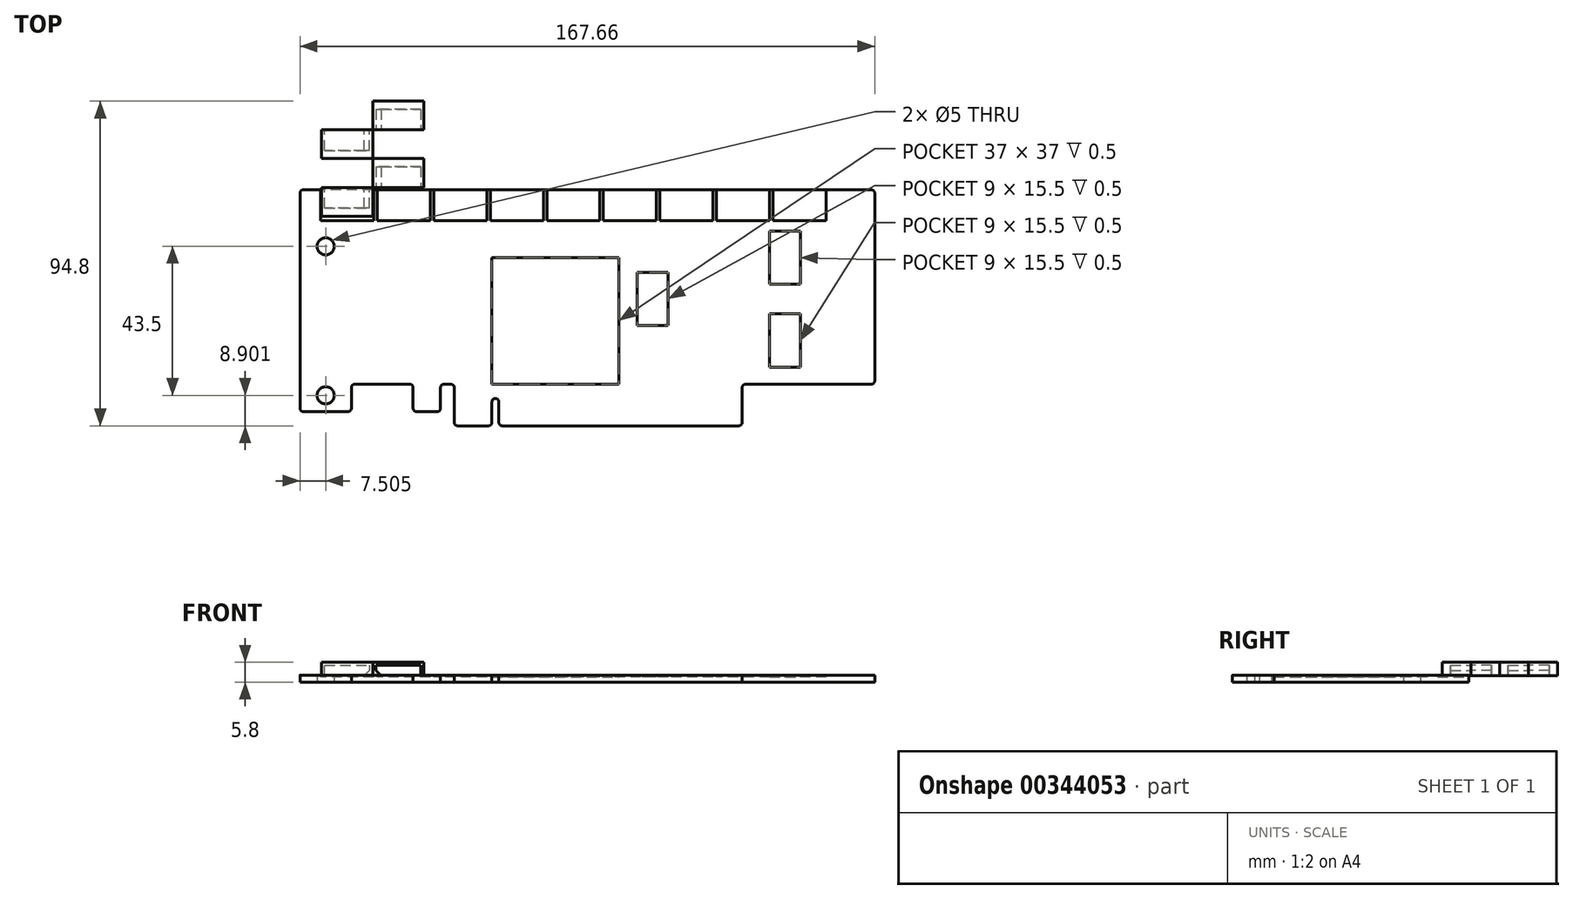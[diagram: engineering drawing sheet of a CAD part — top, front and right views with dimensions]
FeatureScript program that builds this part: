
annotation { "Feature Type Name" : "Feature", "Feature Type Description" : "" }
export const myFeature = defineFeature(function(context is Context, id is Id, definition is map)
    precondition{}
    {
        {
            var Q0;
            Q0=qCreatedBy(makeId("Top.planeOp"),FACE);
            var sketch = newSketch(context, id + "F0", { "sketchPlane" : qUnion([Q0])});
            skLineSegment(sketch, "E0.top", {"start": v(83.83, 32.37) * mm, "end": v(-83.83, 32.37) * mm});
            skLineSegment(sketch, "E0.right", {"start": v(-83.83, -32.37) * mm, "end": v(-83.83, 32.37) * mm});
            skPoint(sketch, "E0.middle", {"position": v(0, 0) * mm});
            skLineSegment(sketch, "E1", {"start": v(-83.83, -32.37) * mm, "end": v(-68.83, -32.37) * mm});
            skLineSegment(sketch, "E2", {"start": v(-68.83, -32.37) * mm, "end": v(-68.83, -24.37) * mm});
            skLineSegment(sketch, "E3", {"start": v(-68.83, -24.37) * mm, "end": v(-50.82, -24.37) * mm});
            skLineSegment(sketch, "E4", {"start": v(-50.82, -24.37) * mm, "end": v(-50.82, -32.37) * mm});
            skLineSegment(sketch, "E5", {"start": v(-50.82, -32.37) * mm, "end": v(-42.83, -32.37) * mm});
            skLineSegment(sketch, "E6", {"start": v(-42.83, -32.37) * mm, "end": v(-42.82, -24.37) * mm});
            skLineSegment(sketch, "E7", {"start": v(-42.82, -24.37) * mm, "end": v(-38.82, -24.37) * mm});
            skLineSegment(sketch, "E8", {"start": v(-38.82, -24.37) * mm, "end": v(-38.82, -36.53) * mm});
            skLineSegment(sketch, "E9", {"start": v(-38.82, -36.53) * mm, "end": v(-27.82, -36.53) * mm});
            skLineSegment(sketch, "E10", {"start": v(-27.82, -36.53) * mm, "end": v(-27.82, -28.53) * mm});
            skLineSegment(sketch, "E11", {"start": v(-27.82, -28.53) * mm, "end": v(-25.82, -28.53) * mm});
            skLineSegment(sketch, "E12", {"start": v(-25.82, -28.53) * mm, "end": v(-25.82, -36.53) * mm});
            skLineSegment(sketch, "E13", {"start": v(-25.82, -36.53) * mm, "end": v(45.18, -36.53) * mm});
            skLineSegment(sketch, "E14", {"start": v(45.18, -36.53) * mm, "end": v(45.18, -24.37) * mm});
            skLineSegment(sketch, "E15", {"start": v(83.83, 32.37) * mm, "end": v(83.83, -24.37) * mm});
            skCircle(sketch, "E16", {"center": v(-76.33, -27.63) * mm, "radius": 2.5 * mm});
            skCircle(sketch, "E17.MirrorC", {"center": v(-76.33, 15.87) * mm, "radius": 2.5 * mm});
            skLineSegment(sketch, "E18", {"start": v(45.18, -24.37) * mm, "end": v(83.82, -24.37) * mm});
            skLineSegment(sketch, "E19", {"start": v(-76.33, 15.87) * mm, "end": v(-76.33, -27.63) * mm, "construction": true});
            skLineSegment(sketch, "E20", {"start": v(-76.33, 15.87) * mm, "end": v(-76.33, 32.37) * mm, "construction": true});
            skLineSegment(sketch, "E21", {"start": v(-83.83, 0) * mm, "end": v(-76.33, 0) * mm, "construction": true});
            skSolve(sketch);
        }
        {
            var Q0;
            Q0=qSketchRegion(id+"F0",true);
            extrude(context, id + "F1", {"entities" : qUnion([Q0]), "depth" : 2 * mm});
        }
        {
            var Q0;
            Q0=makeQuery(id+"F1.opExtrude","CAP_FACE",FACE,{"disambiguationData":[OSD([sQuery(id+"F0.wireOp",EDGE,"E0.top"),sQuery(id+"F0.wireOp",EDGE,"E0.right"),sQuery(id+"F0.wireOp",EDGE,"E1"),sQuery(id+"F0.wireOp",EDGE,"E2"),sQuery(id+"F0.wireOp",EDGE,"E3"),sQuery(id+"F0.wireOp",EDGE,"E4"),sQuery(id+"F0.wireOp",EDGE,"E5"),sQuery(id+"F0.wireOp",EDGE,"E6"),sQuery(id+"F0.wireOp",EDGE,"E7"),sQuery(id+"F0.wireOp",EDGE,"E8"),sQuery(id+"F0.wireOp",EDGE,"E9"),sQuery(id+"F0.wireOp",EDGE,"E10"),sQuery(id+"F0.wireOp",EDGE,"E11"),sQuery(id+"F0.wireOp",EDGE,"E12"),sQuery(id+"F0.wireOp",EDGE,"E13"),sQuery(id+"F0.wireOp",EDGE,"E14"),sQuery(id+"F0.wireOp",EDGE,"E15"),sQuery(id+"F0.wireOp",EDGE,"E16"),sQuery(id+"F0.wireOp",EDGE,"E17.MirrorC"),sQuery(id+"F0.wireOp",EDGE,"E18")])],"isStart":false});
            var sketch = newSketch(context, id + "F2", { "sketchPlane" : qUnion([Q0])});
            skLineSegment(sketch, "E22.bottom", {"start": v(-77.83, 23.37) * mm, "end": v(-62.33, 23.37) * mm});
            skLineSegment(sketch, "E22.top", {"start": v(-77.83, 32.37) * mm, "end": v(-62.33, 32.37) * mm});
            skLineSegment(sketch, "E22.left", {"start": v(-77.83, 23.37) * mm, "end": v(-77.83, 32.37) * mm});
            skLineSegment(sketch, "E22.right", {"start": v(-62.33, 23.37) * mm, "end": v(-62.33, 32.37) * mm});
            skLineSegment(sketch, "E23", {"start": v(-77.83, 32.37) * mm, "end": v(-83.83, 32.37) * mm, "construction": true});
            skLineSegment(sketch, "E24.1.0.0", {"start": v(-61.33, 32.37) * mm, "end": v(-45.83, 32.37) * mm});
            skLineSegment(sketch, "E24.1.0.1", {"start": v(-61.33, 23.37) * mm, "end": v(-61.33, 32.37) * mm});
            skLineSegment(sketch, "E24.1.0.2", {"start": v(-61.33, 23.37) * mm, "end": v(-45.83, 23.37) * mm});
            skLineSegment(sketch, "E24.1.0.3", {"start": v(-45.83, 23.37) * mm, "end": v(-45.83, 32.37) * mm});
            skLineSegment(sketch, "E24.2.0.0", {"start": v(-44.83, 32.37) * mm, "end": v(-29.33, 32.37) * mm});
            skLineSegment(sketch, "E24.2.0.1", {"start": v(-44.83, 23.37) * mm, "end": v(-44.83, 32.37) * mm});
            skLineSegment(sketch, "E24.2.0.2", {"start": v(-44.83, 23.37) * mm, "end": v(-29.33, 23.37) * mm});
            skLineSegment(sketch, "E24.2.0.3", {"start": v(-29.33, 23.37) * mm, "end": v(-29.33, 32.37) * mm});
            skLineSegment(sketch, "E24.direction1", {"start": v(-77.83, 32.37) * mm, "end": v(-61.33, 32.37) * mm, "construction": true});
            skLineSegment(sketch, "E25.0.3.0", {"start": v(-28.33, 32.37) * mm, "end": v(-12.83, 32.37) * mm});
            skLineSegment(sketch, "E25.3.3.0", {"start": v(-28.33, 23.37) * mm, "end": v(-28.33, 32.37) * mm});
            skLineSegment(sketch, "E25.6.3.0", {"start": v(-28.33, 23.37) * mm, "end": v(-12.83, 23.37) * mm});
            skLineSegment(sketch, "E25.9.3.0", {"start": v(-12.83, 23.37) * mm, "end": v(-12.83, 32.37) * mm});
            skLineSegment(sketch, "E25.0.4.0", {"start": v(-11.83, 32.37) * mm, "end": v(3.67, 32.37) * mm});
            skLineSegment(sketch, "E25.3.4.0", {"start": v(-11.83, 23.37) * mm, "end": v(-11.83, 32.37) * mm});
            skLineSegment(sketch, "E25.6.4.0", {"start": v(-11.83, 23.37) * mm, "end": v(3.67, 23.37) * mm});
            skLineSegment(sketch, "E25.9.4.0", {"start": v(3.67, 23.37) * mm, "end": v(3.67, 32.37) * mm});
            skLineSegment(sketch, "E25.0.5.0", {"start": v(4.67, 32.37) * mm, "end": v(20.17, 32.37) * mm});
            skLineSegment(sketch, "E25.3.5.0", {"start": v(4.67, 23.37) * mm, "end": v(4.67, 32.37) * mm});
            skLineSegment(sketch, "E25.6.5.0", {"start": v(4.67, 23.37) * mm, "end": v(20.17, 23.37) * mm});
            skLineSegment(sketch, "E25.9.5.0", {"start": v(20.17, 23.37) * mm, "end": v(20.17, 32.37) * mm});
            skLineSegment(sketch, "E25.0.6.0", {"start": v(21.17, 32.37) * mm, "end": v(36.67, 32.37) * mm});
            skLineSegment(sketch, "E25.3.6.0", {"start": v(21.17, 23.37) * mm, "end": v(21.17, 32.37) * mm});
            skLineSegment(sketch, "E25.6.6.0", {"start": v(21.17, 23.37) * mm, "end": v(36.67, 23.37) * mm});
            skLineSegment(sketch, "E25.9.6.0", {"start": v(36.67, 23.37) * mm, "end": v(36.67, 32.37) * mm});
            skLineSegment(sketch, "E25.0.7.0", {"start": v(37.67, 32.37) * mm, "end": v(53.17, 32.37) * mm});
            skLineSegment(sketch, "E25.3.7.0", {"start": v(37.67, 23.37) * mm, "end": v(37.67, 32.37) * mm});
            skLineSegment(sketch, "E25.6.7.0", {"start": v(37.67, 23.37) * mm, "end": v(53.17, 23.37) * mm});
            skLineSegment(sketch, "E25.9.7.0", {"start": v(53.17, 23.37) * mm, "end": v(53.17, 32.37) * mm});
            skLineSegment(sketch, "E25.0.8.0", {"start": v(54.17, 32.37) * mm, "end": v(69.67, 32.37) * mm});
            skLineSegment(sketch, "E25.3.8.0", {"start": v(54.17, 23.37) * mm, "end": v(54.17, 32.37) * mm});
            skLineSegment(sketch, "E25.6.8.0", {"start": v(54.17, 23.37) * mm, "end": v(69.67, 23.37) * mm});
            skLineSegment(sketch, "E25.9.8.0", {"start": v(69.67, 23.37) * mm, "end": v(69.67, 32.37) * mm});
            skLineSegment(sketch, "E26", {"start": v(53.17, 23.37) * mm, "end": v(53.17, 20.37) * mm, "construction": true});
            skLineSegment(sketch, "E27.bottom", {"start": v(53.17, 20.37) * mm, "end": v(62.17, 20.37) * mm});
            skLineSegment(sketch, "E27.top", {"start": v(53.17, 4.87) * mm, "end": v(62.17, 4.87) * mm});
            skLineSegment(sketch, "E27.left", {"start": v(53.17, 20.37) * mm, "end": v(53.17, 4.87) * mm});
            skLineSegment(sketch, "E27.right", {"start": v(62.17, 20.37) * mm, "end": v(62.17, 4.87) * mm});
            skLineSegment(sketch, "E28.bottom", {"start": v(53.17, -19.37) * mm, "end": v(62.17, -19.37) * mm});
            skLineSegment(sketch, "E28.top", {"start": v(53.17, -3.87) * mm, "end": v(62.17, -3.87) * mm});
            skLineSegment(sketch, "E28.left", {"start": v(53.17, -19.37) * mm, "end": v(53.17, -3.87) * mm});
            skLineSegment(sketch, "E28.right", {"start": v(62.17, -19.37) * mm, "end": v(62.17, -3.87) * mm});
            skLineSegment(sketch, "E29", {"start": v(53.17, 4.87) * mm, "end": v(53.17, -3.87) * mm, "construction": true});
            skLineSegment(sketch, "E30", {"start": v(53.17, -19.37) * mm, "end": v(53.17, -24.37) * mm, "construction": true});
            skLineSegment(sketch, "E31", {"start": v(53.17, 0.5) * mm, "end": v(23.53, 0.5) * mm, "construction": true});
            skLineSegment(sketch, "E32.bottom", {"start": v(23.53, 8.25) * mm, "end": v(14.53, 8.25) * mm});
            skLineSegment(sketch, "E32.top", {"start": v(23.53, -7.25) * mm, "end": v(14.53, -7.25) * mm});
            skLineSegment(sketch, "E32.left", {"start": v(23.53, 8.25) * mm, "end": v(23.53, -7.25) * mm});
            skLineSegment(sketch, "E32.right", {"start": v(14.53, 8.25) * mm, "end": v(14.53, -7.25) * mm});
            skLineSegment(sketch, "E33.bottom", {"start": v(-27.82, -24.37) * mm, "end": v(9.18, -24.37) * mm});
            skLineSegment(sketch, "E33.top", {"start": v(-27.82, 12.63) * mm, "end": v(9.18, 12.63) * mm});
            skLineSegment(sketch, "E33.left", {"start": v(-27.82, -24.37) * mm, "end": v(-27.82, 12.63) * mm});
            skLineSegment(sketch, "E33.right", {"start": v(9.18, -24.37) * mm, "end": v(9.18, 12.63) * mm});
            skLineSegment(sketch, "E34", {"start": v(-38.82, -24.37) * mm, "end": v(-27.82, -24.37) * mm, "construction": true});
            skSolve(sketch);
        }
        {
            var Q0;
            Q0=makeQuery(id+"F1.opExtrude","SWEPT_EDGE",EDGE,{"disambiguationData":[OSD([sQuery(id+"F0.wireOp",EDGE,"E0.right"),sQuery(id+"F0.wireOp",EDGE,"E1")])]});
            var Q1;
            Q1=makeQuery(id+"F1.opExtrude","SWEPT_EDGE",EDGE,{"disambiguationData":[OSD([sQuery(id+"F0.wireOp",EDGE,"E1"),sQuery(id+"F0.wireOp",EDGE,"E2")])]});
            var Q2;
            Q2=makeQuery(id+"F1.opExtrude","SWEPT_EDGE",EDGE,{"disambiguationData":[OSD([sQuery(id+"F0.wireOp",EDGE,"E2"),sQuery(id+"F0.wireOp",EDGE,"E3")])]});
            var Q3;
            Q3=makeQuery(id+"F1.opExtrude","SWEPT_EDGE",EDGE,{"disambiguationData":[OSD([sQuery(id+"F0.wireOp",EDGE,"E4"),sQuery(id+"F0.wireOp",EDGE,"E5")])]});
            var Q4;
            Q4=makeQuery(id+"F1.opExtrude","SWEPT_EDGE",EDGE,{"disambiguationData":[OSD([sQuery(id+"F0.wireOp",EDGE,"E5"),sQuery(id+"F0.wireOp",EDGE,"E6")])]});
            var Q5;
            Q5=makeQuery(id+"F1.opExtrude","SWEPT_EDGE",EDGE,{"disambiguationData":[OSD([sQuery(id+"F0.wireOp",EDGE,"E6"),sQuery(id+"F0.wireOp",EDGE,"E7")])]});
            var Q6;
            Q6=makeQuery(id+"F1.opExtrude","SWEPT_EDGE",EDGE,{"disambiguationData":[OSD([sQuery(id+"F0.wireOp",EDGE,"E8"),sQuery(id+"F0.wireOp",EDGE,"E9")])]});
            var Q7;
            Q7=makeQuery(id+"F1.opExtrude","SWEPT_EDGE",EDGE,{"disambiguationData":[OSD([sQuery(id+"F0.wireOp",EDGE,"E9"),sQuery(id+"F0.wireOp",EDGE,"E10")])]});
            var Q8;
            Q8=makeQuery(id+"F1.opExtrude","SWEPT_EDGE",EDGE,{"disambiguationData":[OSD([sQuery(id+"F0.wireOp",EDGE,"E10"),sQuery(id+"F0.wireOp",EDGE,"E11")])]});
            var Q9;
            Q9=makeQuery(id+"F1.opExtrude","SWEPT_EDGE",EDGE,{"disambiguationData":[OSD([sQuery(id+"F0.wireOp",EDGE,"E12"),sQuery(id+"F0.wireOp",EDGE,"E13")])]});
            var Q10;
            Q10=makeQuery(id+"F1.opExtrude","SWEPT_EDGE",EDGE,{"disambiguationData":[OSD([sQuery(id+"F0.wireOp",EDGE,"E15"),sQuery(id+"F0.wireOp",EDGE,"E18")])]});
            var Q11;
            Q11=makeQuery(id+"F1.opExtrude","SWEPT_EDGE",EDGE,{"disambiguationData":[OSD([sQuery(id+"F0.wireOp",EDGE,"E14"),sQuery(id+"F0.wireOp",EDGE,"E18")])]});
            var Q12;
            Q12=makeQuery(id+"F1.opExtrude","SWEPT_EDGE",EDGE,{"disambiguationData":[OSD([sQuery(id+"F0.wireOp",EDGE,"E13"),sQuery(id+"F0.wireOp",EDGE,"E14")])]});
            var Q13;
            Q13=makeQuery(id+"F1.opExtrude","SWEPT_EDGE",EDGE,{"disambiguationData":[OSD([sQuery(id+"F0.wireOp",EDGE,"E0.top"),sQuery(id+"F0.wireOp",EDGE,"E15")])]});
            var Q14;
            Q14=makeQuery(id+"F1.opExtrude","SWEPT_EDGE",EDGE,{"disambiguationData":[OSD([sQuery(id+"F0.wireOp",EDGE,"E0.top"),sQuery(id+"F0.wireOp",EDGE,"E0.right")])]});
            var Q15;
            Q15=makeQuery(id+"F1.opExtrude","SWEPT_EDGE",EDGE,{"disambiguationData":[OSD([sQuery(id+"F0.wireOp",EDGE,"E3"),sQuery(id+"F0.wireOp",EDGE,"E4")])]});
            var Q16;
            Q16=makeQuery(id+"F1.opExtrude","SWEPT_EDGE",EDGE,{"disambiguationData":[OSD([sQuery(id+"F0.wireOp",EDGE,"E7"),sQuery(id+"F0.wireOp",EDGE,"E8")])]});
            var Q17;
            Q17=makeQuery(id+"F1.opExtrude","SWEPT_EDGE",EDGE,{"disambiguationData":[OSD([sQuery(id+"F0.wireOp",EDGE,"E11"),sQuery(id+"F0.wireOp",EDGE,"E12")])]});
            fillet(context, id + "F3", {"entities" : qUnion([Q0, Q1, Q2, Q3, Q4, Q5, Q6, Q7, Q8, Q9, Q10, Q11, Q12, Q13, Q14, Q15, Q16, Q17]), "radius" : 1 * mm, "tangentPropagation" : true, "allowEdgeOverflow" : false});
        }
        {
            var Q0;
            Q0 = qSketchRegion(id + "F2", true);
            extrude(context, id + "F4", {"entities" : qUnion([Q0]), "operationType" : NewBodyOperationType.REMOVE, "oppositeDirection" : true, "depth" : .5 * mm});
        }
        {
            var Q0;
            Q0=makeQuery(id+"F4.boolean.opBoolean","COPY",FACE,{"derivedFrom":makeQuery(id+"F4.opExtrude","CAP_FACE",FACE,{"disambiguationData":[OSD([sQuery(id+"F2.wireOp",EDGE,"E22.bottom"),sQuery(id+"F2.wireOp",EDGE,"E22.top"),sQuery(id+"F2.wireOp",EDGE,"E22.left"),sQuery(id+"F2.wireOp",EDGE,"E22.right")])],"isStart":false})});
            cPlane(context, id + "F5", {"entities" : qUnion([Q0]), "cplaneType" : CPlaneType.OFFSET, "offset" : .3 * mm, "width" : 150 * mm, "height" : 150 * mm});
        }
        {
            var Q0;
            Q0=qCreatedBy(id+"F5.planeOp",FACE);
            var sketch = newSketch(context, id + "F6", { "sketchPlane" : qUnion([Q0])});
            skLineSegment(sketch, "E35.0", {"start": v(-77.83, 23.37) * mm, "end": v(-77.83, 32.37) * mm, "construction": true});
            skLineSegment(sketch, "E36.0", {"start": v(-77.83, 23.37) * mm, "end": v(-62.33, 23.37) * mm, "construction": true});
            skLineSegment(sketch, "E37.0", {"start": v(-62.33, 23.37) * mm, "end": v(-62.33, 32.37) * mm, "construction": true});
            skLineSegment(sketch, "E38.0", {"start": v(-62.33, 32.37) * mm, "end": v(-77.83, 32.37) * mm, "construction": true});
            skLineSegment(sketch, "E39.0", {"start": v(-62.63, 32.07) * mm, "end": v(-77.53, 32.07) * mm});
            skLineSegment(sketch, "E39.1", {"start": v(-62.63, 23.67) * mm, "end": v(-62.63, 32.07) * mm});
            skLineSegment(sketch, "E39.2", {"start": v(-77.53, 23.67) * mm, "end": v(-62.63, 23.67) * mm});
            skLineSegment(sketch, "E39.3", {"start": v(-77.53, 23.67) * mm, "end": v(-77.53, 32.07) * mm});
            skSolve(sketch);
        }
        {
            var Q0;
            Q0 = qSketchRegion(id + "F6", true);
            extrude(context, id + "F7", {"entities" : qUnion([Q0]), "depth" : 4 * mm});
        }
        {
            var Q0;
            Q0=makeQuery(id+"F7.opExtrude","SWEPT_FACE",FACE,{"disambiguationData":[OSD([sQuery(id+"F6.wireOp",EDGE,"E39.0")])]});
            var sketch = newSketch(context, id + "F8", { "sketchPlane" : qUnion([Q0])});
            skLineSegment(sketch, "E40", {"start": v(76.63, 1.8) * mm, "end": v(76.63, 4.9) * mm});
            skLineSegment(sketch, "E41", {"start": v(76.63, 4.9) * mm, "end": v(63.53, 4.9) * mm});
            skLineSegment(sketch, "E42", {"start": v(63.53, 4.9) * mm, "end": v(63.53, 3.4) * mm});
            skLineSegment(sketch, "E43", {"start": v(63.53, 3.4) * mm, "end": v(65.13, 1.8) * mm});
            skLineSegment(sketch, "E44", {"start": v(65.13, 1.8) * mm, "end": v(76.63, 1.8) * mm});
            skLineSegment(sketch, "E45", {"start": v(70.08, 5.8) * mm, "end": v(70.08, 4.9) * mm, "construction": true});
            skSolve(sketch);
        }
        {
            var Q0;
            Q0 = qSketchRegion(id + "F8", true);
            extrude(context, id + "F9", {"entities" : qUnion([Q0]), "operationType" : NewBodyOperationType.REMOVE, "oppositeDirection" : true, "depth" : 6 * mm});
        }
        {
            var Q0;
            Q0=makeQuery(id+"F7.opExtrude","SWEPT_BODY",BODY,{"disambiguationData":[OSD([sQuery(id+"F6.wireOp",EDGE,"E39.0"),sQuery(id+"F6.wireOp",EDGE,"E39.1"),sQuery(id+"F6.wireOp",EDGE,"E39.2"),sQuery(id+"F6.wireOp",EDGE,"E39.3")])]});
            transform(context, id + "F10", {"entities" : qUnion([Q0]), "transformType" : TransformType.TRANSLATION_3D, "dx" : 0 * mm, "dy" : 1 * mm, "dz" : 0 * mm, "makeCopy" : false});
        }
        {
            var Q0;
            Q0=makeQuery(id+"F7.opExtrude","SWEPT_BODY",BODY,{"disambiguationData":[OSD([sQuery(id+"F6.wireOp",EDGE,"E39.0"),sQuery(id+"F6.wireOp",EDGE,"E39.1"),sQuery(id+"F6.wireOp",EDGE,"E39.2"),sQuery(id+"F6.wireOp",EDGE,"E39.3")])]});
            var Q1;
            Q1=makeQuery(id+"F7.opExtrude","SWEPT_EDGE",EDGE,{"disambiguationData":[OSD([sQuery(id+"F6.wireOp",EDGE,"E39.0"),sQuery(id+"F6.wireOp",EDGE,"E39.1")])]});
            transform(context, id + "F11", {"entities" : qUnion([Q0]), "transformType" : TransformType.ROTATION, "transformAxis" : qUnion([Q1]), "angle" : 180 * degree, "makeCopy" : true});
        }
        {
            var Q0;
            Q0=makeQuery(id+"F11.opPattern","COPY",BODY,{"derivedFrom":makeQuery(id+"F7.opExtrude","SWEPT_BODY",BODY,{"disambiguationData":[OSD([sQuery(id+"F6.wireOp",EDGE,"E39.0"),sQuery(id+"F6.wireOp",EDGE,"E39.1"),sQuery(id+"F6.wireOp",EDGE,"E39.2"),sQuery(id+"F6.wireOp",EDGE,"E39.3")])]}),"instanceName":"1"});
            var Q1;
            Q1=makeQuery(id+"F11.opPattern","COPY",EDGE,{"derivedFrom":makeQuery(id+"F7.opExtrude","SWEPT_EDGE",EDGE,{"disambiguationData":[OSD([sQuery(id+"F6.wireOp",EDGE,"E39.1"),sQuery(id+"F6.wireOp",EDGE,"E39.2")])]}),"instanceName":"1"});
            transform(context, id + "F12", {"entities" : qUnion([Q0]), "transformType" : TransformType.ROTATION, "transformAxis" : qUnion([Q1]), "angle" : 180 * degree, "makeCopy" : true});
        }
        {
            var Q0;
            Q0=makeQuery(id+"F12.opPattern","COPY",BODY,{"derivedFrom":makeQuery(id+"F11.opPattern","COPY",BODY,{"derivedFrom":makeQuery(id+"F7.opExtrude","SWEPT_BODY",BODY,{"disambiguationData":[OSD([sQuery(id+"F6.wireOp",EDGE,"E39.0"),sQuery(id+"F6.wireOp",EDGE,"E39.1"),sQuery(id+"F6.wireOp",EDGE,"E39.2"),sQuery(id+"F6.wireOp",EDGE,"E39.3")])]}),"instanceName":"1"}),"instanceName":"1"});
            var Q1;
            Q1=makeQuery(id+"F12.opPattern","COPY",EDGE,{"derivedFrom":makeQuery(id+"F11.opPattern","COPY",EDGE,{"derivedFrom":makeQuery(id+"F7.opExtrude","SWEPT_EDGE",EDGE,{"disambiguationData":[OSD([sQuery(id+"F6.wireOp",EDGE,"E39.0"),sQuery(id+"F6.wireOp",EDGE,"E39.1")])]}),"instanceName":"1"}),"instanceName":"1"});
            transform(context, id + "F13", {"entities" : qUnion([Q0]), "transformType" : TransformType.ROTATION, "transformAxis" : qUnion([Q1]), "angle" : 180 * degree, "makeCopy" : true});
        }
    });
